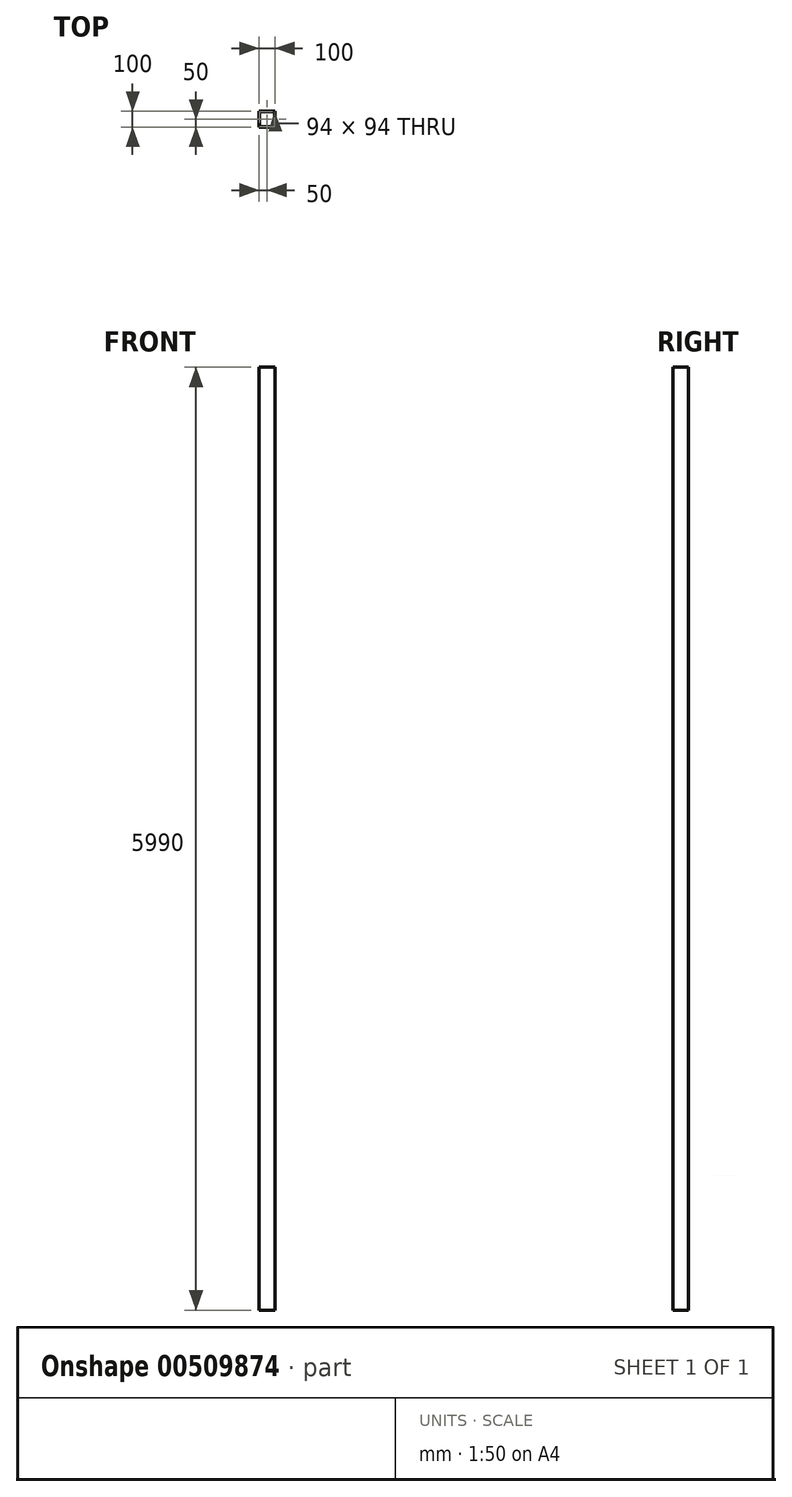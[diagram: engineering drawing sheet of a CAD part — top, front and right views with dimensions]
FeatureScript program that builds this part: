
annotation { "Feature Type Name" : "Feature", "Feature Type Description" : "" }
export const myFeature = defineFeature(function(context is Context, id is Id, definition is map)
    precondition{}
    {
        {
            var Q0;
            Q0=qCreatedBy(makeId("Top.planeOp"),FACE);
            var sketch = newSketch(context, id + "F0", { "sketchPlane" : qUnion([Q0])});
            skLineSegment(sketch, "E0.bottom", {"start": v(50, -50) * mm, "end": v(-50, -50) * mm});
            skLineSegment(sketch, "E0.top", {"start": v(50, 50) * mm, "end": v(-50, 50) * mm});
            skLineSegment(sketch, "E0.left", {"start": v(50, -50) * mm, "end": v(50, 50) * mm});
            skLineSegment(sketch, "E0.right", {"start": v(-50, -50) * mm, "end": v(-50, 50) * mm});
            skPoint(sketch, "E0.middle", {"position": v(0, 0) * mm});
            skLineSegment(sketch, "E1.bottom", {"start": v(47, -47) * mm, "end": v(-47, -47) * mm});
            skLineSegment(sketch, "E1.top", {"start": v(47, 47) * mm, "end": v(-47, 47) * mm});
            skLineSegment(sketch, "E1.left", {"start": v(47, -47) * mm, "end": v(47, 47) * mm});
            skLineSegment(sketch, "E1.right", {"start": v(-47, -47) * mm, "end": v(-47, 47) * mm});
            skSolve(sketch);
        }
        {
            var Q0;
            Q0 = qSketchRegion(id + "F0", true);
            extrude(context, id + "F1", {"entities" : qUnion([Q0]), "depth" : 5990 * mm});
        }
    });
